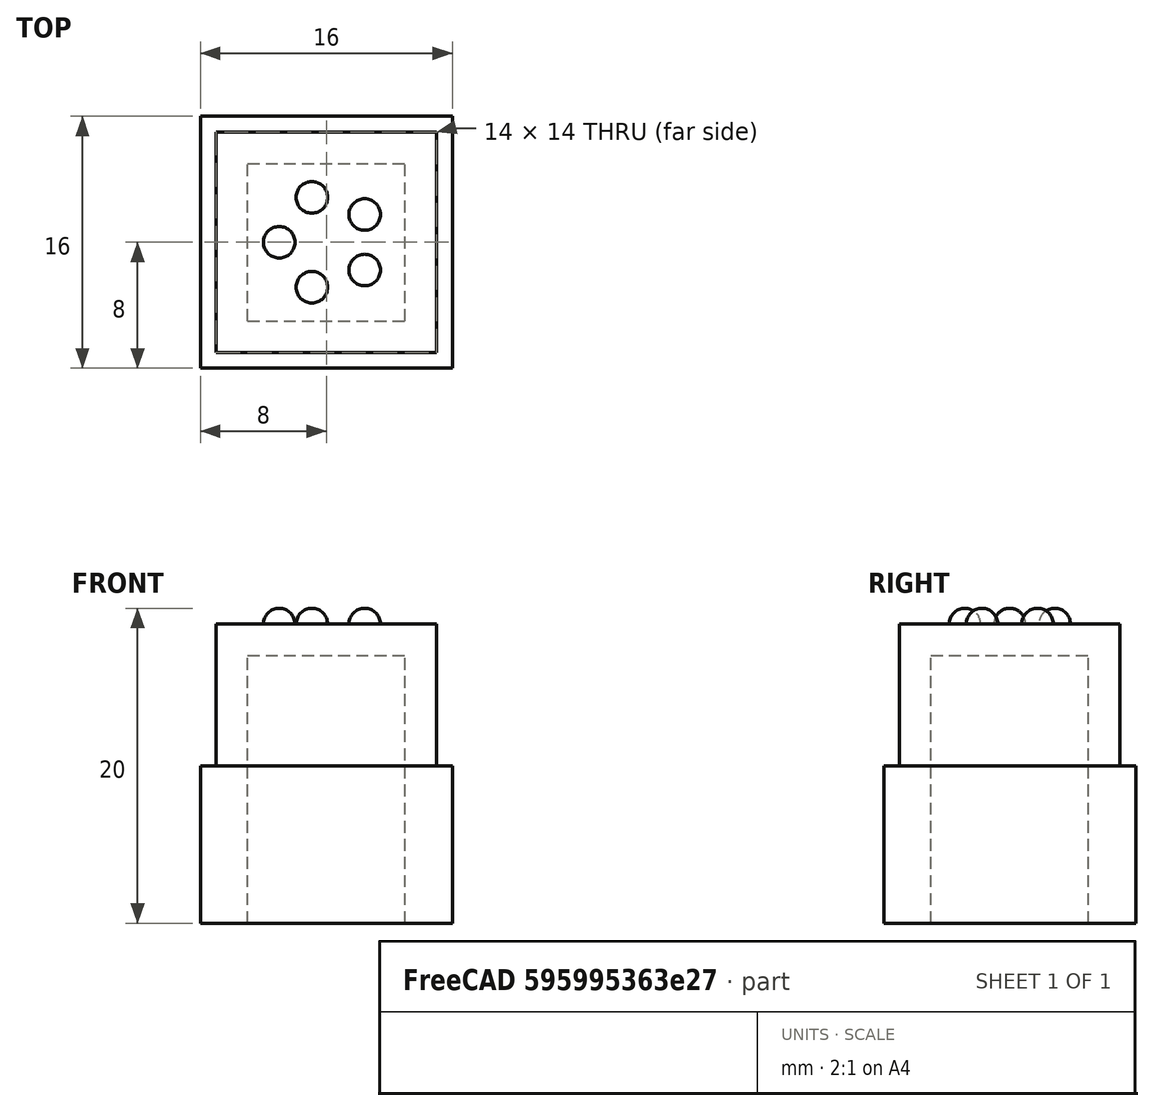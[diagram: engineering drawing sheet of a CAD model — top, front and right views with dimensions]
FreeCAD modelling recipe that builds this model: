
FCSTD DOCUMENT  (FreeCAD 0.18.3R)
Label: dots
License: All rights reserved
LicenseURL: http://en.wikipedia.org/wiki/All_rights_reserved
objects: Part::Box×2, PartDesign::AdditiveBox×1, PartDesign::AdditiveSphere×1, PartDesign::PolarPattern×1, PartDesign::Boolean×1, PartDesign::Body×1, Part::Cut×1
note: 10 computed .brp shape members not serialized (recipe doc carries the construction recipe); baked Part::Feature solids carry a one-line shape summary decoded from their .brp

FEATURE [Part::Box] Box  label="Cube"
  AttacherType = Attacher::AttachEngine3D
  Height = 10
  Length = 16
  Placement = pos=(-8,-8,0) rot=(0,0,1;0rad)
  Width = 16
FEATURE [PartDesign::AdditiveBox] Box002
  AttacherType = Attacher::AttachEngine3D
  AttachmentOffset = pos=(-7,-7,0) rot=(0,0,1;0rad)
  Height = 19
  Length = 14
  MapMode = 5
  Placement = pos=(-7,-7,0) rot=(0,0,1;0rad)
  Support = -> [XY_Plane]
  Width = 14
FEATURE [PartDesign::AdditiveSphere] Sphere001
  Angle1 = -90
  Angle2 = 90
  Angle3 = 360
  AttacherType = Attacher::AttachEngine3D
  AttachmentOffset = pos=(-3,0,19) rot=(0,0,1;0rad)
  BaseFeature = -> Box002
  MapMode = 5
  Placement = pos=(-3,0,19) rot=(0,0,1;0rad)
  Radius = 1
  Support = -> [XY_Plane]
FEATURE [PartDesign::PolarPattern] PolarPattern
  Angle = 360
  Axis = -> Z_Axis
  BaseFeature = -> Sphere001
  Occurrences = 5
  Originals = -> [Sphere001]
  Placement = pos=(-3,0,19) rot=(0,0,1;0rad)
FEATURE [PartDesign::Boolean] Boolean
  BaseFeature = -> PolarPattern
  Group = -> [Box]
  Type = 0
FEATURE [PartDesign::Body] Body
  Group = -> [Box002,Sphere001,PolarPattern,Boolean]
  Origin = -> Origin
  Tip = -> Boolean
FEATURE [Part::Box] Box003  label="Cube001"
  AttacherType = Attacher::AttachEngine3D
  Height = 17
  Length = 10
  Placement = pos=(-5,-5,0) rot=(0,0,1;0rad)
  Width = 10
FEATURE [Part::Cut] Cut
  Base = -> Body
  Tool = -> Box003
